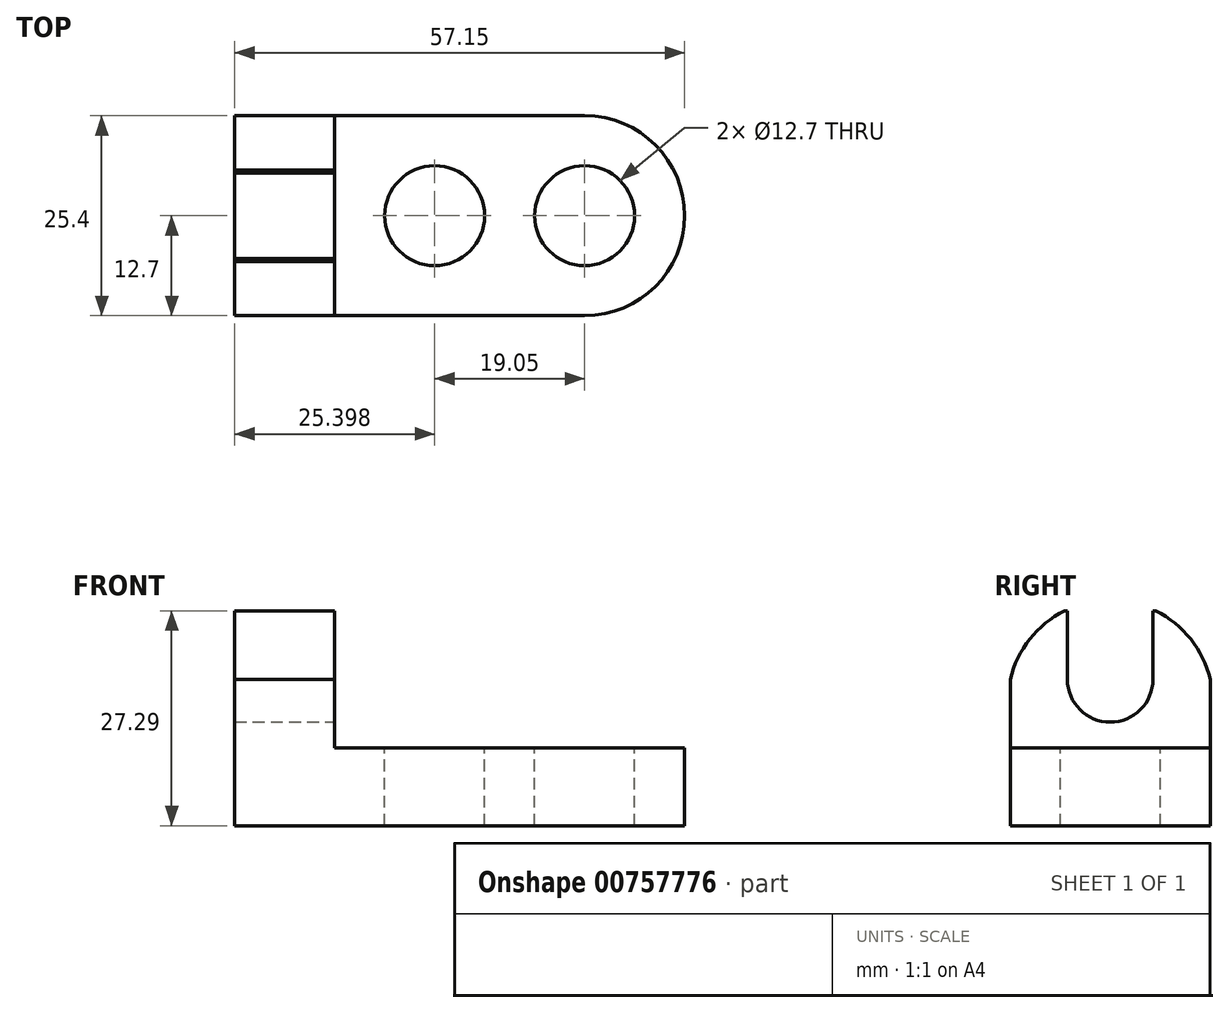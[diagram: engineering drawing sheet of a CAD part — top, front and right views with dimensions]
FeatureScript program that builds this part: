
annotation { "Feature Type Name" : "Feature", "Feature Type Description" : "" }
export const myFeature = defineFeature(function(context is Context, id is Id, definition is map)
    precondition{}
    {
        {
            var Q0;
            Q0=qCreatedBy(makeId("Front.planeOp"),FACE);
            var sketch = newSketch(context, id + "F0", { "sketchPlane" : qUnion([Q0])});
            skLineSegment(sketch, "E0", {"start": v(27.45, 0) * mm, "end": v(-29.7, 0) * mm});
            skLineSegment(sketch, "E1", {"start": v(-29.7, 0) * mm, "end": v(-29.7, 27.29) * mm});
            skLineSegment(sketch, "E2", {"start": v(-29.7, 27.29) * mm, "end": v(-17, 27.29) * mm});
            skLineSegment(sketch, "E3", {"start": v(-17, 27.29) * mm, "end": v(-17, 9.9) * mm});
            skLineSegment(sketch, "E4", {"start": v(-17, 9.9) * mm, "end": v(27.45, 9.9) * mm});
            skLineSegment(sketch, "E5", {"start": v(27.45, 9.9) * mm, "end": v(27.45, 0) * mm});
            skSolve(sketch);
        }
        {
            var Q0;
            Q0 = qSketchRegion(id + "F0", true);
            extrude(context, id + "F1", {"entities" : qUnion([Q0]), "depth" : 25.4 * mm, "offsetDistance" : 25.4 * mm});
        }
        {
            var Q0;
            Q0=makeQuery(id+"F1.opExtrude","SWEPT_FACE",FACE,{"disambiguationData":[OSD([sQuery(id+"F0.wireOp",EDGE,"E3")])]});
            var sketch = newSketch(context, id + "F2", { "sketchPlane" : qUnion([Q0])});
            skLineSegment(sketch, "E6", {"start": v(-25.4, 18.6) * mm, "end": v(0, 18.6) * mm});
            skCircle(sketch, "E7", {"center": v(-12.7, 18.6) * mm, "radius": 5.43 * mm});
            skLineSegment(sketch, "E8", {"start": v(-7.27, 18.6) * mm, "end": v(-7.27, 27.29) * mm});
            skLineSegment(sketch, "E9", {"start": v(-18.13, 18.6) * mm, "end": v(-18.13, 27.29) * mm});
            skArc(sketch, "E10", {"start": v(0, 18.6) * mm, "mid": v(-12.7, 28.65) * mm, "end": v(-25.4, 18.6) * mm});
            skSolve(sketch);
        }
        {
            var Q0;
            {var subQ0=sQuery(id+"F2.wireOp",EDGE,"E7");var subQ1=sQuery(id+"F2.wireOp",EDGE,"E6");var subQ2=makeQuery(id+"F2.imprint","INTERSECT",VERTEX,{"derivedFrom":[subQ1,subQ0,sQuery(id+"F2.wireOp",EDGE,"E8")]});Q0=makeQuery(id+"F2.imprint","IMPRINT",FACE,{"disambiguationData":[TD([[makeQuery(id+"F2.imprint","IMPRINT",EDGE,{"disambiguationData":[TD([[subQ2,1.0]])],"derivedFrom":subQ1}),1.0]])]});}
            var Q1;
            {var subQ0=sQuery(id+"F2.wireOp",EDGE,"E7");var subQ1=sQuery(id+"F2.wireOp",EDGE,"E6");var subQ2=makeQuery(id+"F2.imprint","INTERSECT",VERTEX,{"derivedFrom":[subQ1,subQ0,sQuery(id+"F2.wireOp",EDGE,"E8")]});Q1=makeQuery(id+"F2.imprint","IMPRINT",FACE,{"disambiguationData":[TD([[makeQuery(id+"F2.imprint","IMPRINT",EDGE,{"disambiguationData":[TD([[subQ2,1.0]])],"derivedFrom":subQ1}),-1.0]])]});}
            var Q2;
            {var subQ0=sQuery(id+"F2.wireOp",EDGE,"E8");Q2=makeQuery(id+"F2.imprint","IMPRINT",FACE,{"disambiguationData":[TD([[makeQuery(id+"F2.imprint","IMPRINT",EDGE,{"derivedFrom":subQ0}),1.0]])]});}
            var Q3;
            {var subQ0=sQuery(id+"F2.wireOp",EDGE,"E10");var subQ1=makeQuery(id+"F1.opExtrude","SWEPT_EDGE",EDGE,{"disambiguationData":[OSD([sQuery(id+"F0.wireOp",EDGE,"E2"),sQuery(id+"F0.wireOp",EDGE,"E3")])]});var subQ2=makeQuery(id+"F2.imprint","INTERSECT",VERTEX,{"disambiguationData":[OD(0.0)],"derivedFrom":[subQ1,subQ0]});Q3=makeQuery(id+"F2.imprint","IMPRINT",FACE,{"disambiguationData":[TD([[makeQuery(id+"F2.imprint","IMPRINT",EDGE,{"disambiguationData":[TD([[subQ2,-1.0]])],"derivedFrom":subQ0}),1.0]])]});}
            var Q4;
            {var subQ0=sQuery(id+"F2.wireOp",EDGE,"E10");var subQ1=sQuery(id+"F0.wireOp",EDGE,"E3");var subQ2=makeQuery(id+"F1.opExtrude","CAP_EDGE",EDGE,{"disambiguationData":[OSD([subQ1])],"isStart":false});var subQ3=makeQuery(id+"F2.imprint","INTERSECT",VERTEX,{"derivedFrom":[subQ2,sQuery(id+"F2.wireOp",EDGE,"E6"),subQ0]});Q4=makeQuery(id+"F2.imprint","IMPRINT",FACE,{"disambiguationData":[TD([[makeQuery(id+"F2.imprint","IMPRINT",EDGE,{"disambiguationData":[TD([[subQ3,1.0]])],"derivedFrom":subQ0}),-1.0]])]});}
            var Q5;
            {var subQ0=sQuery(id+"F2.wireOp",EDGE,"E10");var subQ1=sQuery(id+"F0.wireOp",EDGE,"E3");var subQ2=makeQuery(id+"F1.opExtrude","CAP_EDGE",EDGE,{"disambiguationData":[OSD([subQ1])],"isStart":true});var subQ3=makeQuery(id+"F2.imprint","INTERSECT",VERTEX,{"derivedFrom":[subQ2,sQuery(id+"F2.wireOp",EDGE,"E6"),subQ0]});Q5=makeQuery(id+"F2.imprint","IMPRINT",FACE,{"disambiguationData":[TD([[makeQuery(id+"F2.imprint","IMPRINT",EDGE,{"disambiguationData":[TD([[subQ3,-1.0]])],"derivedFrom":subQ0}),-1.0]])]});}
            extrude(context, id + "F3", {"entities" : qUnion([Q0, Q1, Q2, Q3, Q4, Q5]), "operationType" : NewBodyOperationType.REMOVE, "endBound" : BoundingType.THROUGH_ALL, "oppositeDirection" : true, "depth" : 25.4 * mm, "offsetDistance" : 25.4 * mm});
        }
        {
            var Q0;
            Q0=makeQuery(id+"F1.opExtrude","SWEPT_FACE",FACE,{"disambiguationData":[OSD([sQuery(id+"F0.wireOp",EDGE,"E4")])]});
            var sketch = newSketch(context, id + "F4", { "sketchPlane" : qUnion([Q0])});
            skLineSegment(sketch, "E11", {"start": v(14.75, 0) * mm, "end": v(14.75, -25.4) * mm});
            skLineSegment(sketch, "E12", {"start": v(-4.3, 0) * mm, "end": v(-4.3, -25.4) * mm});
            skCircle(sketch, "E13", {"center": v(14.75, -12.7) * mm, "radius": 6.35 * mm});
            skCircle(sketch, "E14", {"center": v(-4.3, -12.7) * mm, "radius": 6.35 * mm});
            skArc(sketch, "E15", {"start": v(14.75, -25.4) * mm, "mid": v(27.45, -12.7) * mm, "end": v(14.75, 0) * mm});
            skSolve(sketch);
        }
        {
            var Q0;
            {var subQ0=sQuery(id+"F4.wireOp",EDGE,"E13");var subQ1=sQuery(id+"F4.wireOp",EDGE,"E11");var subQ2=makeQuery(id+"F4.imprint","INTERSECT",VERTEX,{"disambiguationData":[OD(0.0)],"derivedFrom":[subQ1,subQ0]});Q0=makeQuery(id+"F4.imprint","IMPRINT",FACE,{"disambiguationData":[TD([[makeQuery(id+"F4.imprint","IMPRINT",EDGE,{"disambiguationData":[TD([[subQ2,-1.0]])],"derivedFrom":subQ1}),-1.0]])]});}
            var Q1;
            {var subQ0=sQuery(id+"F4.wireOp",EDGE,"E13");var subQ1=sQuery(id+"F4.wireOp",EDGE,"E11");var subQ2=makeQuery(id+"F4.imprint","INTERSECT",VERTEX,{"disambiguationData":[OD(0.0)],"derivedFrom":[subQ1,subQ0]});Q1=makeQuery(id+"F4.imprint","IMPRINT",FACE,{"disambiguationData":[TD([[makeQuery(id+"F4.imprint","IMPRINT",EDGE,{"disambiguationData":[TD([[subQ2,-1.0]])],"derivedFrom":subQ1}),1.0]])]});}
            var Q2;
            {var subQ0=sQuery(id+"F4.wireOp",EDGE,"E14");var subQ1=sQuery(id+"F4.wireOp",EDGE,"E12");var subQ2=makeQuery(id+"F4.imprint","INTERSECT",VERTEX,{"disambiguationData":[OD(0.0)],"derivedFrom":[subQ1,subQ0]});Q2=makeQuery(id+"F4.imprint","IMPRINT",FACE,{"disambiguationData":[TD([[makeQuery(id+"F4.imprint","IMPRINT",EDGE,{"disambiguationData":[TD([[subQ2,-1.0]])],"derivedFrom":subQ1}),-1.0]])]});}
            var Q3;
            {var subQ0=sQuery(id+"F4.wireOp",EDGE,"E14");var subQ1=sQuery(id+"F4.wireOp",EDGE,"E12");var subQ2=makeQuery(id+"F4.imprint","INTERSECT",VERTEX,{"disambiguationData":[OD(0.0)],"derivedFrom":[subQ1,subQ0]});Q3=makeQuery(id+"F4.imprint","IMPRINT",FACE,{"disambiguationData":[TD([[makeQuery(id+"F4.imprint","IMPRINT",EDGE,{"disambiguationData":[TD([[subQ2,-1.0]])],"derivedFrom":subQ1}),1.0]])]});}
            var Q4;
            {var subQ0=sQuery(id+"F4.wireOp",EDGE,"E15");var subQ1=sQuery(id+"F0.wireOp",EDGE,"E4");var subQ2=makeQuery(id+"F1.opExtrude","CAP_EDGE",EDGE,{"disambiguationData":[OSD([subQ1])],"isStart":true});var subQ3=makeQuery(id+"F4.imprint","INTERSECT",VERTEX,{"derivedFrom":[subQ2,sQuery(id+"F4.wireOp",EDGE,"E11"),subQ0]});Q4=makeQuery(id+"F4.imprint","IMPRINT",FACE,{"disambiguationData":[TD([[makeQuery(id+"F4.imprint","IMPRINT",EDGE,{"disambiguationData":[TD([[subQ3,1.0]])],"derivedFrom":subQ0}),-1.0]])]});}
            var Q5;
            {var subQ0=sQuery(id+"F4.wireOp",EDGE,"E15");var subQ1=sQuery(id+"F0.wireOp",EDGE,"E4");var subQ2=makeQuery(id+"F1.opExtrude","CAP_EDGE",EDGE,{"disambiguationData":[OSD([subQ1])],"isStart":false});var subQ3=makeQuery(id+"F4.imprint","INTERSECT",VERTEX,{"derivedFrom":[subQ2,sQuery(id+"F4.wireOp",EDGE,"E11"),subQ0]});Q5=makeQuery(id+"F4.imprint","IMPRINT",FACE,{"disambiguationData":[TD([[makeQuery(id+"F4.imprint","IMPRINT",EDGE,{"disambiguationData":[TD([[subQ3,-1.0]])],"derivedFrom":subQ0}),-1.0]])]});}
            extrude(context, id + "F5", {"entities" : qUnion([Q0, Q1, Q2, Q3, Q4, Q5]), "operationType" : NewBodyOperationType.REMOVE, "endBound" : BoundingType.THROUGH_ALL, "oppositeDirection" : true, "depth" : 25.4 * mm, "offsetDistance" : 25.4 * mm});
        }
    });
